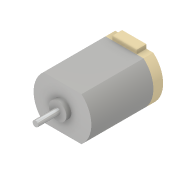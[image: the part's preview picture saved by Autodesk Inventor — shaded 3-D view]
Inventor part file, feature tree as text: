
AUTODESK INVENTOR PART (.ipt)
format: ipt  version: 2017 (Build 210142000, 142)  size: 167,424 bytes
history: native  units: in
note: dims shown in document units (in); Inventor stores cm internally (conversion verified against a paired STEP export)
features: extrude x7, sketch x7, projected_geometry x1
ambient origin geometry x8: Origin, YZ Plane, XZ Plane, XY Plane, X Axis, Y Axis, Z Axis, Center Point
bodies: Solid1 (feature_tree)
feature tree (15):
  extrude  "Extrusion1"  Depth=0.5945in
  extrude  "Extrusion2"  Depth=0.9843in
  extrude  "Extrusion3"  Depth=0.0669in
  extrude  "Extrusion4"  Depth=0.3937in
  extrude  "Extrusion5"  Depth=0.3346in
  extrude  "Extrusion6"  Depth=0.1339in TaperAngle=0.0deg
  extrude  "Extrusion7"  Depth=0.05in TaperAngle=0.0deg
  sketch  "Sketch1"  dims[d0=0.7913in d1=0.5945in]
  sketch  "Sketch2"  dims[d2=0.9843in d3=0.0in d4=0.2421in]
  sketch  "Sketch3"  dims[d5=0.0669in d6=0.0in d7=0.0787in]
  sketch  "Sketch4"  dims[d8=0.3031in d9=0.0in d10=0.3937in]
  sketch  "Sketch5"  dims[d11=0.0906in d12=0.0in d13=0.3346in]
  sketch  "Sketch6"  dims[d14=0.0551in d15=0.1339in d16=0.0in]
  projected_geometry  "Projected Loop1"
  sketch  "Sketch7"  dims[d17=0.0in d18=1.0in d19=0.0in d20=0.05in d21=0.0in]
